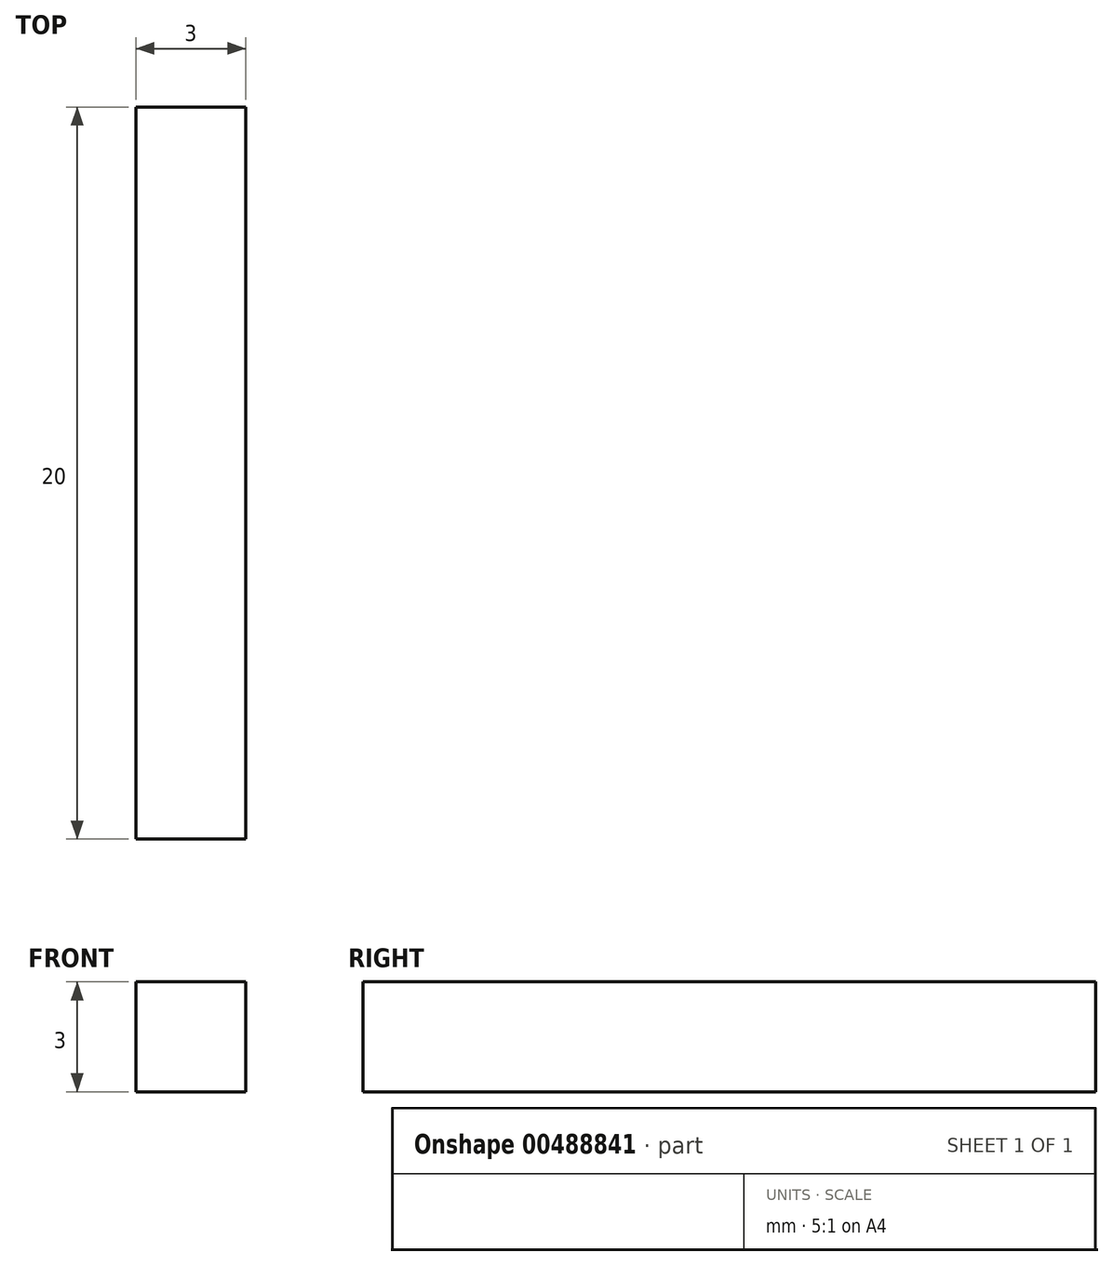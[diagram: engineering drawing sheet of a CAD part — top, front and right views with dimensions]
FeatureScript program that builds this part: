
annotation { "Feature Type Name" : "Feature", "Feature Type Description" : "" }
export const myFeature = defineFeature(function(context is Context, id is Id, definition is map)
    precondition{}
    {
        {
            var Q0;
            Q0=qCreatedBy(makeId("Front.planeOp"),FACE);
            var sketch = newSketch(context, id + "F0", { "sketchPlane" : qUnion([Q0])});
            skLineSegment(sketch, "E0.bottom", {"start": v(-1.5, 1.5) * mm, "end": v(1.5, 1.5) * mm});
            skLineSegment(sketch, "E0.top", {"start": v(-1.5, -1.5) * mm, "end": v(1.5, -1.5) * mm});
            skLineSegment(sketch, "E0.left", {"start": v(-1.5, 1.5) * mm, "end": v(-1.5, -1.5) * mm});
            skLineSegment(sketch, "E0.right", {"start": v(1.5, 1.5) * mm, "end": v(1.5, -1.5) * mm});
            skSolve(sketch);
        }
        {
            var Q0;
            Q0 = qSketchRegion(id + "F0", true);
            extrude(context, id + "F1", {"entities" : qUnion([Q0]), "depth" : 20 * mm});
        }
    });
